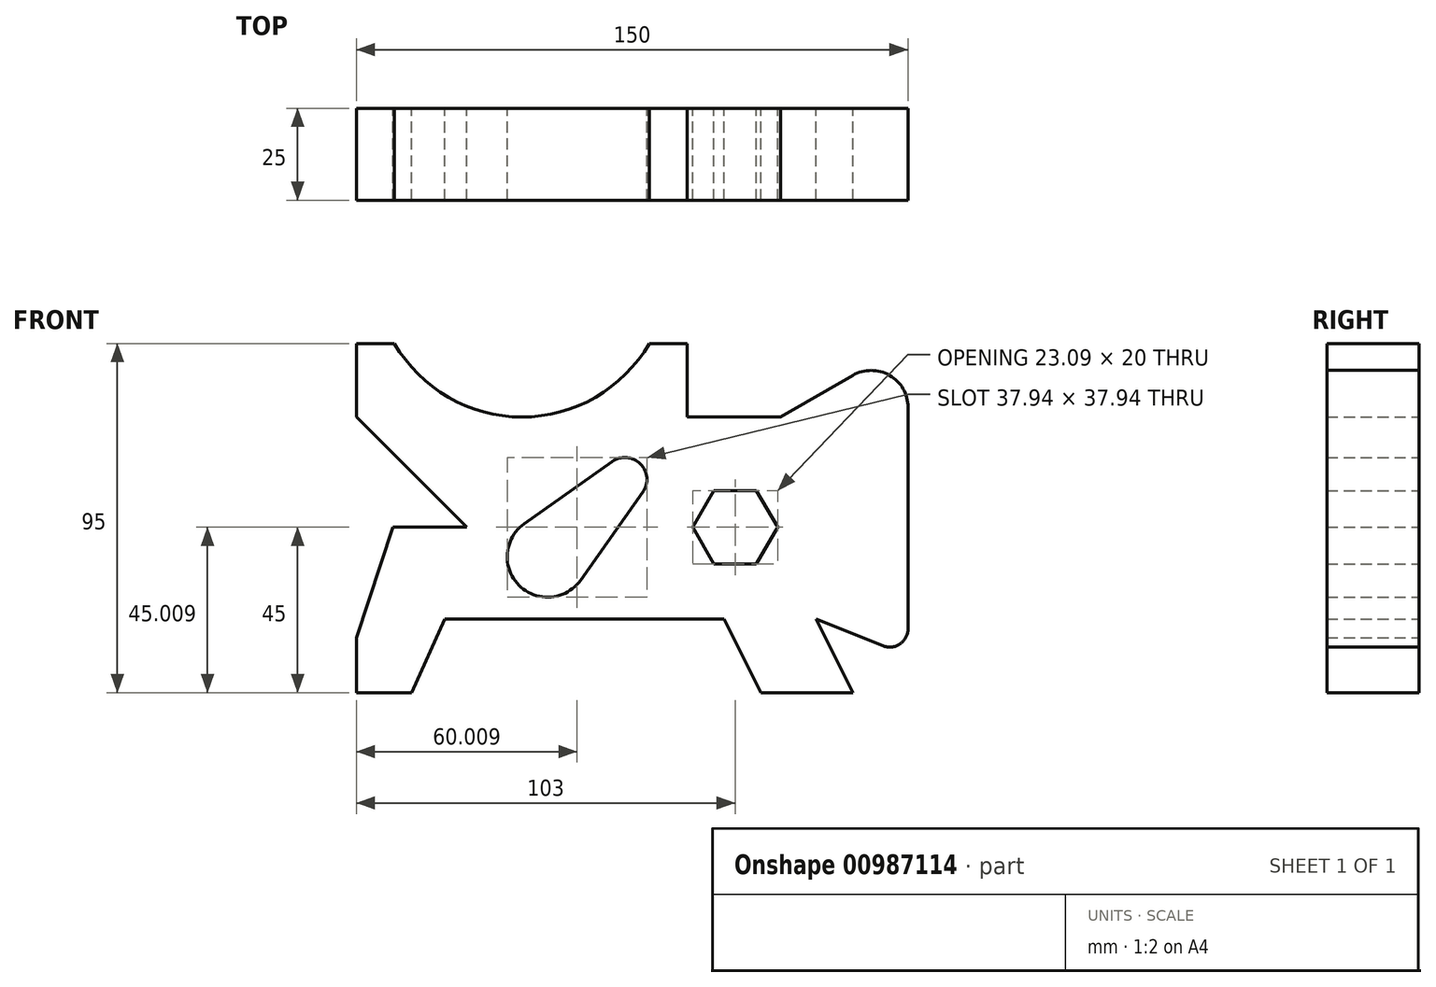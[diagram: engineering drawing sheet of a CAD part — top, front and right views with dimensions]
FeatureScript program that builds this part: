
annotation { "Feature Type Name" : "Feature", "Feature Type Description" : "" }
export const myFeature = defineFeature(function(context is Context, id is Id, definition is map)
    precondition{}
    {
        {
            var Q0;
            Q0=qCreatedBy(makeId("Front.planeOp"),FACE);
            var sketch = newSketch(context, id + "F0", { "sketchPlane" : qUnion([Q0])});
            skLineSegment(sketch, "E0", {"start": v(0, 0) * mm, "end": v(15, 0) * mm});
            skLineSegment(sketch, "E1", {"start": v(15, 0) * mm, "end": v(24, 20) * mm});
            skLineSegment(sketch, "E2", {"start": v(24, 20) * mm, "end": v(100, 20) * mm});
            skLineSegment(sketch, "E3", {"start": v(100, 20) * mm, "end": v(110, 0) * mm});
            skLineSegment(sketch, "E4", {"start": v(110, 0) * mm, "end": v(135, 0) * mm});
            skLineSegment(sketch, "E5", {"start": v(150, 17.39) * mm, "end": v(150, 77.68) * mm});
            skLineSegment(sketch, "E6", {"start": v(135, 86.34) * mm, "end": v(115.36, 75) * mm});
            skLineSegment(sketch, "E7", {"start": v(0, 95) * mm, "end": v(0, 75) * mm});
            skLineSegment(sketch, "E8", {"start": v(0, 75) * mm, "end": v(30, 45) * mm});
            skLineSegment(sketch, "E9", {"start": v(30, 45) * mm, "end": v(10, 45) * mm});
            skLineSegment(sketch, "E10", {"start": v(10, 45) * mm, "end": v(0, 15) * mm});
            skLineSegment(sketch, "E11", {"start": v(90, 95) * mm, "end": v(90, 75) * mm});
            skLineSegment(sketch, "E12", {"start": v(0, 95) * mm, "end": v(10.36, 95) * mm});
            skLineSegment(sketch, "E13", {"start": v(90, 75) * mm, "end": v(115.36, 75) * mm});
            skLineSegment(sketch, "E14", {"start": v(0, 15) * mm, "end": v(0, 0) * mm});
            skPoint(sketch, "E15.visualSharp", {"position": v(150, 95) * mm});
            skArc(sketch, "E16.filletArc", {"start": v(150, 77.68) * mm, "mid": v(145, 86.34) * mm, "end": v(135, 86.34) * mm});
            skArc(sketch, "E17", {"start": v(10.36, 95) * mm, "mid": v(45, 75) * mm, "end": v(79.64, 95) * mm});
            skLineSegment(sketch, "E18.trimOffspring", {"start": v(79.64, 95) * mm, "end": v(90, 95) * mm});
            skArc(sketch, "E19", {"start": v(45.64, 45.98) * mm, "mid": v(44.22, 29.22) * mm, "end": v(60.98, 30.64) * mm});
            skArc(sketch, "E20", {"start": v(77.9, 54.53) * mm, "mid": v(77.24, 62.24) * mm, "end": v(69.53, 62.9) * mm});
            skLineSegment(sketch, "E21", {"start": v(135, 0) * mm, "end": v(125, 20) * mm});
            skLineSegment(sketch, "E22", {"start": v(45.64, 45.98) * mm, "end": v(69.53, 62.9) * mm});
            skLineSegment(sketch, "E23", {"start": v(60.98, 30.64) * mm, "end": v(77.9, 54.53) * mm});
            skLineSegment(sketch, "E24", {"start": v(125, 20) * mm, "end": v(143.14, 12.74) * mm});
            skPoint(sketch, "E25.visualSharp", {"position": v(150, 10) * mm});
            skArc(sketch, "E25.filletArc", {"start": v(143.14, 12.74) * mm, "mid": v(147.8, 13.24) * mm, "end": v(150, 17.39) * mm});
            skCircle(sketch, "E26.cCircle", {"center": v(103, 45) * mm, "radius": 10 * mm, "construction": true});
            skLineSegment(sketch, "E26.0", {"start": v(108.77, 35) * mm, "end": v(97.23, 35) * mm});
            skLineSegment(sketch, "E26.1", {"start": v(97.23, 35) * mm, "end": v(91.45, 45) * mm});
            skLineSegment(sketch, "E26.2", {"start": v(91.45, 45) * mm, "end": v(97.23, 55) * mm});
            skLineSegment(sketch, "E26.3", {"start": v(97.23, 55) * mm, "end": v(108.77, 55) * mm});
            skLineSegment(sketch, "E26.4", {"start": v(108.77, 55) * mm, "end": v(114.55, 45) * mm});
            skLineSegment(sketch, "E26.5", {"start": v(114.55, 45) * mm, "end": v(108.77, 35) * mm});
            skPoint(sketch, "E26.0.midPoint", {"position": v(103, 35) * mm});
            skSolve(sketch);
        }
        {
            var Q0;
            Q0 = qSketchRegion(id + "F0", true);
            extrude(context, id + "F1", {"entities" : qUnion([Q0]), "depth" : 25 * mm, "offsetDistance" : 25 * mm});
        }
    });
